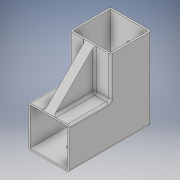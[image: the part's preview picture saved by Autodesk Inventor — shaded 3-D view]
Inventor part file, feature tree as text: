
AUTODESK INVENTOR PART (.ipt)
format: ipt  version: 2019.4 (Build 234330000, 330)  size: 189,440 bytes
history: native  units: mm
features: extrude x5, sketch x4, hole x2, chamfer x1, fillet x1
ambient origin geometry x8: Origin, YZ Plane, XZ Plane, XY Plane, X Axis, Y Axis, Z Axis, Center Point
bodies: Solid1 (feature_tree)
feature tree (13):
  sketch  "Sketch1"  dims[d0=41.0mm d1=41.0mm]
  extrude  "Extrusion1"  Depth=41.0mm
  extrude  "Extrusion2"  Depth=45.0mm
  sketch  "Sketch2"  dims[d2=45.0mm d3=45.0mm]
  extrude  "Extrusion3"  Depth=2.5mm TaperAngle=0.0deg
  extrude  "Extrusion4"  Depth=45.0mm
  extrude  "Extrusion5"  Depth=41.0mm
  chamfer  "Chamfer1"  Distance=41.0mm
  hole  "Hole1"  [1 undecoded]
  hole  "Hole2"  [1 undecoded]
  fillet  "Fillet1"  Radius=5.0mm
  sketch  "Sketch3"  dims[d4=90.0mm d5=0.0mm d6=2.5mm d7=0.0mm]
  sketch  "Sketch5"  dims[d8=45.0mm d9=45.0mm d10=41.0mm d11=41.0mm d12=45.0mm d13=0.0mm d14=40.0mm d15=0.0mm d16=5.0mm d17=10.0mm d18=45.0mm d19=0.0mm d20=45.0mm d21=2.0mm d22=45.0deg d23=5.0mm d24=6.0mm d25=4.0mm d26=2.0mm d27=90.0deg d28=8.0mm d29=20.594885mm d32=5.0mm d33=6.0mm d34=4.0mm d35=2.0mm d36=90.0deg d37=8.0mm d38=20.594885mm d39=2.5mm]
note: 2 required parameter values undecoded (feature->parameter linkage not recoverable at this tier; creation-order binding heuristic only, values carry confidence <= 0.55)
